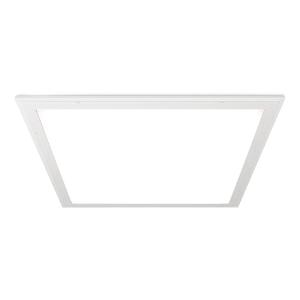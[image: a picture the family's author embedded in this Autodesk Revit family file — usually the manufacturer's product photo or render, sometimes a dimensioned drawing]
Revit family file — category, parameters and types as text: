
# Revit family: 3f_filippi_-_l_650_luce_diffusa_vss_3f_filippi_-_21884_-_l_650_42w-840_dali_vss_599x599
name_source: partatom
category: Lighting Fixtures
units: mm (PartAtom-declared; Revit-internal decimal feet)

## family parameters
Cut with Voids When Loaded = No
Host = Face
Light Source = No
Part Type = Normal
Room Calculation Point = No
Round Connector Dimension = Use Diameter
Shared = No

## types (1)
- 3F Filippi - L 650 Luce Diffusa VSS (1 x LED, 4965 lm, 47 W, 4000 K)
    Apparent Load = 47 VA
    Approval mark = ENEC
    CIE Flux Codes = 63 92 98 100 100
    Color Rendering = 80
    Color Temperature = 4000 K
    Control Gear = Electronic transformer
    Default Elevation = 1800 mm
    Description = ILLUMINOTECHNICAL
Luminous efficiency 100% (DLOR 100%, ULOR 0%).
Initial luminous flux of the luminaire 4965 lm.
Direct symmetric distribution.
Installation Interdistance Transv.D = 1.17 x hu - Long.D = 1.16 x hu.
Average luminance <3000 cd/m² for radial angles >65°.
Tabular UGR (CIE 117 - 4H-8H; S=0.25H; 70/50/20): RUG 18 - 17.8.
Beam angle: 90° - 88°.
Luminous efficacy 106 lm/W.
Lifetime (L93/B10): 30000 h. (tq+25°C)
Lifetime (L90/B10): 50000 h. (tq+25°C)
Lifetime (L85/B10): 80000 h. (tq+25°C)
Lifetime (L80/B10): 100000 h. (tq+25°C)
Sudden decreased luminous flux after 50000 hours: 0% (C0).
Photobiological safety in compliance with IEC/TR 62778: RG0 risk exempt, (IEC 62471).
In compliance with IEC/EN 62722-2-1 - IEC/EN 62717 standards.

SOURCE
Squared LED module 42W/840.
Source with special protection against aggressive chemically-volatile substances for standard LED technology.
Energy efficiency class (UE 2019/2020 - UE 2019/2015): D.
CIE 13.3 Colour rendering index: CRI >80 (R9 <50%).
IES TM-30 Fidelity Index: Rf = 84 Rg = 95.
CCT nominal colour temperature 4000 K.
Colour initial tolerance (MacAdam): SDCM 3.

MECHANICAL
Housing in galvannealed steel, painted in white epoxy-polyester.
Perimetral frame in white stainless steel.
VSS moulded laminated dipped glass, non-combustible, thickness 7 mm.
Anti-glare opal polycarbonate filter for brightness uniformity.
The version 599x599 is dedicated to modular metal false ceilings with dimensions of 600x600.
Luminaire with limited surface temperature. - D - (EN 60598-2-24)
Dimensions: 599x599 mm, height 90 mm. Weight 10.28 kg.
IP66 protection degree for exposed part, IP64 for recessed part.
Mechanical strength to impacts IK08 (5 joule).
Glow-wire test resistance 650°C.

ELECTRICAL
Halogen Free DALI-2 DATI (Parts 251, 252, 253), PUSH-DIM, electronic wiring 230V-50/60Hz, power factor 0.95 at full load, THD <25%, constant output current, SELV, class I, 1 driver, 1 DALI addresse.
Power of the luminaire 47 W.
CE - IEC 60598-1 - EN 60598-1.
SAFE FLICKER: PstLM=<1 and SVM=<0.4 (IEC TR 61547-1 and IEC TR 63158), to ensure a more comfortable and safe light.
Luminaire compliant with EN 60598-2-22 for power supply from a centralised emergency system CPSS (Central Power Supply System), not incorporated in the luminaire - high risk areas excluded. The default power and flux are 100% in AC and 15% in DC.
Ambient temperature from 0°C to +40°C.
Temperature class T6 max 85°C.
5-pole terminal block (L-N-PE-DA/DA) quick connection for line connection with connection capacity 2x2.5 mm² per poles.
Relative humidity UR: <85%.

INSTALLATION
Trimless recessed fitting, to be used with inspectable false-ceilings that can be inspected using fixing brackets which are always required, also designed for the hanging from rough ceiling.
All accessories dedicated to this product are available on the Catalog and on our website www.3F-Filippi.com.

APPLICATIONS
Suitable product for food production plants (HACCP), IFS (Food Version 6), BRC (GSFS Food Version 7).
Environments: hospital premises, transit areas, laboratories, platform-roof, underpasses.
Environments: sterilized, aseptic.
In hospital environments, food industry or machines with parts in motion, with considerable sudden temperature changes, and in general in any environments requiring total protection against falling fragments, use luminaires with laminated glass only.
Tempered glass is not immune to falling fragments from harmless and caused by shocks or exceptionally derived from the tempering process.
Environments requiring a high level of protection and simplified cleaning.
Environments with exacting visual tasks, where diffused soft light for optimum visual comfort is required.

LIGHT MANAGEMENT
Recommended minimum setting: 10%.
The luminaire, equipped with (DALI-2 DATI) driver, can be controlled manually with 3F Easy Dim technology or automatically/manually with wired or wireless DALI/D2D control systems.
The D2D driver guarantees interoperability with other devices with the same certification by making the following information available:
Device Data (Part 251), Energy Report (Part 252), Diagnosis & Maintenance (Part 253).
In electrical systems without a regulation system (manual or automatic) and DALI bus, a suitable jumper must be made on the DA-DA terminals of the appliance.

WARNING
Luminaire designed for disposal/recycling at end-of-life.
Replaceable (LED only) light source by a professional. Replaceable control gear by a professional.
    Height = 0 mm  [stored 0 ft]
    Lamp = 1 x LED
    Lamp Light Flux = 4965 lm
    Lamp Power = 47 W
    Lamp count = 1
    Length = 599 mm
    Lifetime = 50000 h
    Luminous efficacy = 106 lm/W
    Manufacturer = 3F Filippi
    ModVariant = No
    Model = 3F Filippi - 21884 - L 650 42W-840 DALI VSS 599x599
    Mounting Place = Ceiling
    Mounting Type = Recessed
    Number of Poles = 1
    OnlyDefault = Yes
    Power Factor = 1
    Product Name = 3F Filippi - L 650 Luce Diffusa VSS
    Product group = recessed luminaire
    ProductGroupID = 4
    Protection Class = Protection class I
    Protection Degree = IP 64
    RLX_Detail_Level = 1
    RLX_Emergency_Light_Flux = 0 lm
    RLX_Emergency_Type = 0
    RLX_Emergency_Type_DB = No
    RlxData = <blob elided: 100845 chars, md5=87127e79>
    Socket = socket
    Standby Power = 0 W
    System Light Flux = 4965 lm
    System Power = 47 W
    Type Comments = Product without accessories
    Type Image = 3ffilippi_l_650_luce_diffusa_vss.jpg
    URL = http://relux.com
    VarID = ---
    Voltage = 0 V
    Weight = 0.00 kg
    Width = 599 mm

note: [stored X ft] marks values corroborated as IEEE doubles in the binary element streams (Revit-internal decimal feet)

## geometry (parser evidence)
native form markers: Blend x4, Sweep x10
no freeform markers — native parametric forms only
